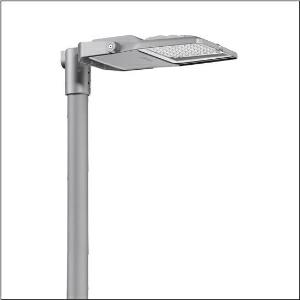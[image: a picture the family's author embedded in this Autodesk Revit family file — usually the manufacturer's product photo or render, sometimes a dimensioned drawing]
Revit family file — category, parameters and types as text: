
# Revit family: floodlight_fl_21_iq_mini___pl43_5xa7772d2a3a_1f0e
name_source: partatom
category: Lighting Fixtures
units: mm (PartAtom-declared; Revit-internal decimal feet)

## family parameters
Cut with Voids When Loaded = No
Host = Face
Light Source = No
Part Type = Normal
Room Calculation Point = No
Round Connector Dimension = Use Diameter
Shared = No

## types (1)
- --- (1 x LED, 18290 lm, 143 W, 3000K)
    Apparent Load = 143 VA
    CIE Flux Codes = 27 78 99 100 100
    Color Rendering = 70
    Color Temperature = 3000K
    Default Elevation = 1800 mm
    Description = Floodlight FL 21 iQ mini, floodlight, primary light control with lens, of PMMA, primary optical cover: protective disc, of toughened safety glass, transparent, light distribution: PL43, light emission: direct distribution, installation type: surface-mounted, LED, High Power LED, rated luminous flux: 18.290lm, luminous efficacy: 128lm/W, light colour: 730, colour temperature: 3000K, control: Auto-Match, Temp-Guard, Night-Set, Smart-Wire, Desk-Remote (wireless, voltage-free reading and setting of iQ features in the workshop via application-optimized NFC function/RFID function), optimised constant luminous flux control (CLO 2.0), Light-Fading, Lumen-Switch, with terminal, 6-pole, mains connection: 220..240V, AC, 50/60Hz, start of lifetime: 143W, end of service life: 152W, reduction: 61W, luminaire housing, of diecast aluminium, powder-coated, Siteco® metallic grey (DB 702S), corrosivity category C5 mid according to DIN EN ISO 12944, sealing non-destructively replaceable, please order mast flange separately, mast bracket, of steel, galvanised, powder-coated, protection rating (complete): IP66, insulation class (complete): insulation class II (safety insulation), certification: CE, ENEC, VDE, protection symbol: D, impact resistance: IK08, permissible operating ambient temperature: -40..+40°C, permissible operating ambient temperature for outdoor applications: -40..+50°C, standard: DIN EN 12944, LABS conformity tested according to VDMA 24364:2018-05, packaging unit: 1 piece

Light Distribution: PL43
    Height = 70 mm
    Lamp = 1 x LED
    Lamp Light Flux = 18290 lm
    Lamp Power = 143 W
    Lamp count = 1
    Length = 485 mm
    Luminous efficacy = 128 lm/W
    Manufacturer = Siteco
    ModVariant = No
    Model = 5XA7772D2A3A
    Number of Poles = 1
    OnlyDefault = Yes
    Power Factor = 1
    Product Name = Floodlight FL 21 iQ mini | PL43
    Product group = floodlight | pylon annexe
    ProductGroupID = 6200
    Protection Class = Protection class II
    Protection Degree = IP 66
    RLX_Detail_Level = 1
    RLX_Emergency_Light_Flux = 0 lm
    RLX_Emergency_Type = 0
    RLX_Emergency_Type_DB = No
    RlxData = <blob elided: 101449 chars, md5=9718a19d>
    Socket = socket
    Standby Power = 0 W
    System Light Flux = 18290 lm
    System Power = 143 W
    Type Comments = factory setting: luminous flux: 100 % | dim-lin: 254 | 730 mA
    Type Image = l_1007125.jpg
    URL = http://relux.com
    VarID = @adj_111775
    Voltage = 0 V
    Weight = 0.00 kg
    Width = 337 mm

## geometry (parser evidence)
native form markers: Blend x4, Sweep x14
no freeform markers — native parametric forms only
